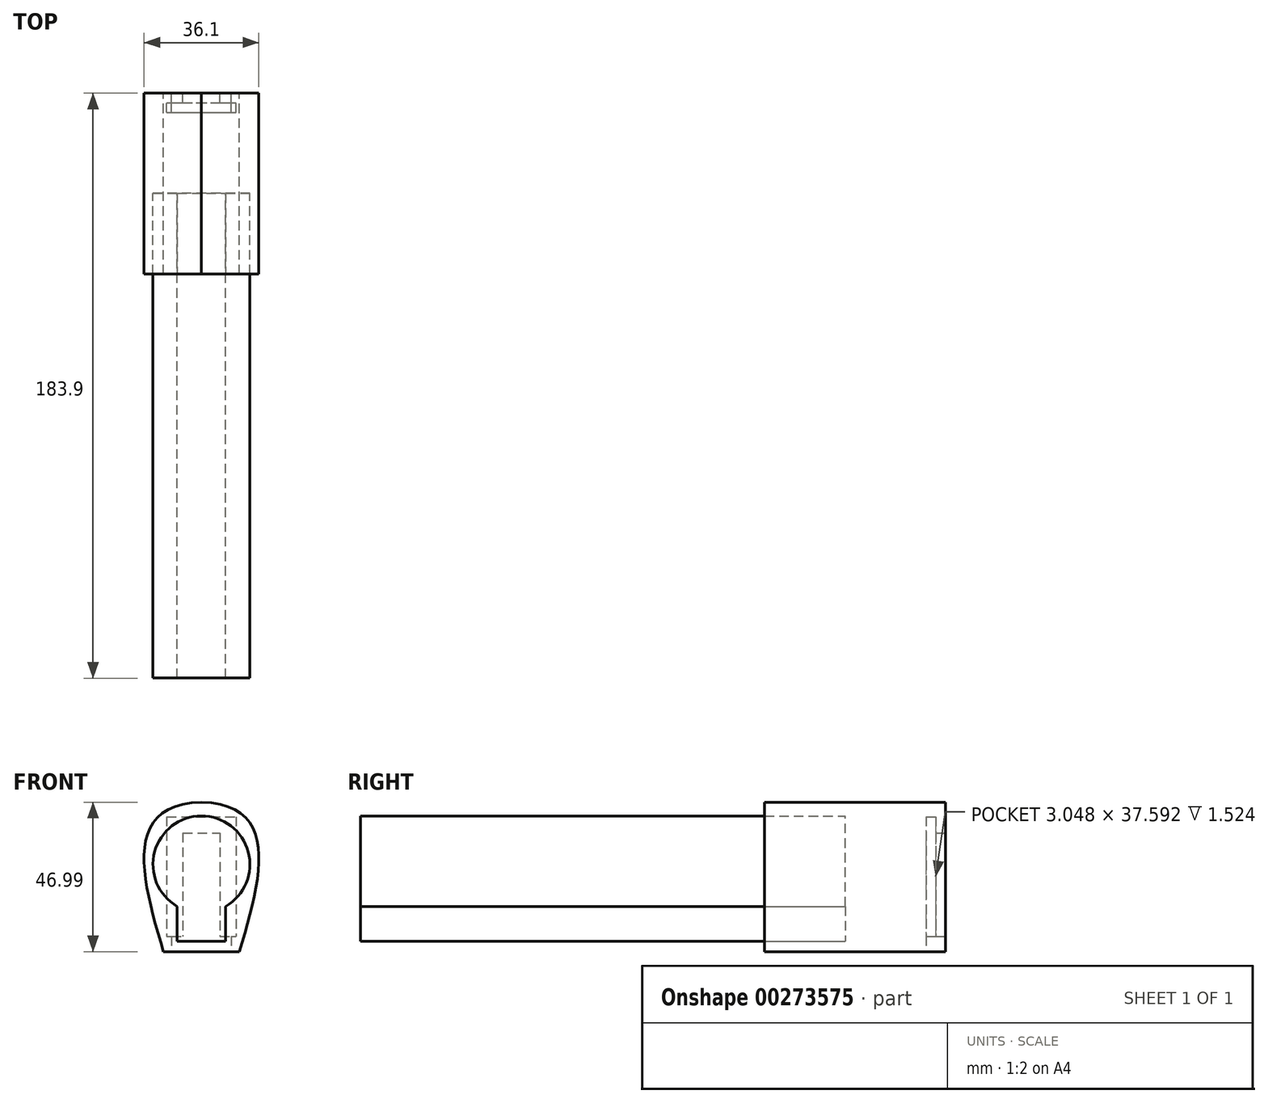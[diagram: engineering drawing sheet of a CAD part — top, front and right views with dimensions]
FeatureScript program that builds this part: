
annotation { "Feature Type Name" : "Feature", "Feature Type Description" : "" }
export const myFeature = defineFeature(function(context is Context, id is Id, definition is map)
    precondition{}
    {
        {
            var Q0;
            Q0=qCreatedBy(makeId("Front.planeOp"),FACE);
            var sketch = newSketch(context, id + "F0", { "sketchPlane" : qUnion([Q0])});
            skLineSegment(sketch, "E0.bottom", {"start": v(-5.84, 16.26) * mm, "end": v(5.84, 16.26) * mm});
            skLineSegment(sketch, "E0.top", {"start": v(-5.84, -16.26) * mm, "end": v(5.84, -16.26) * mm});
            skLineSegment(sketch, "E0.left", {"start": v(-5.84, 16.26) * mm, "end": v(-5.84, -16.26) * mm});
            skLineSegment(sketch, "E0.right", {"start": v(5.84, 16.26) * mm, "end": v(5.84, -16.26) * mm});
            skPoint(sketch, "E0.middle", {"position": v(0, 0) * mm});
            skLineSegment(sketch, "E1.bottom", {"start": v(-9.4, -16.26) * mm, "end": v(9.4, -16.26) * mm});
            skLineSegment(sketch, "E1.top", {"start": v(-9.4, -21.08) * mm, "end": v(9.4, -21.08) * mm});
            skLineSegment(sketch, "E1.left", {"start": v(-9.4, -16.26) * mm, "end": v(-9.4, -21.08) * mm});
            skLineSegment(sketch, "E1.right", {"start": v(9.4, -16.26) * mm, "end": v(9.4, -21.08) * mm});
            skPoint(sketch, "E1.middle", {"position": v(0, -18.67) * mm});
            skLineSegment(sketch, "E2", {"start": v(-8.6, 25.9) * mm, "end": v(11.39, 25.9) * mm, "construction": true});
            skLineSegment(sketch, "E3", {"start": v(-9.4, -21.08) * mm, "end": v(-11.94, -21.08) * mm});
            skFitSpline(sketch, "E4", {"points": [v(-11.94, -21.08) * mm, v(0, 25.9) * mm], "startDerivative": vector(-19.85, 66.84) * mm, "endDerivative": vector(76.2, 2.26) * mm});
            skFitSpline(sketch, "E5.MirrorCS", {"points": [v(11.94, -21.08) * mm, v(0, 25.9) * mm], "startDerivative": vector(19.85, 66.84) * mm, "endDerivative": vector(-76.2, 2.26) * mm});
            skLineSegment(sketch, "E6.MirrorCS", {"start": v(9.4, -21.08) * mm, "end": v(11.94, -21.08) * mm});
            skSolve(sketch);
        }
        {
            var Q0;
            Q0=makeQuery(id+"F0.imprint","IMPRINT",FACE,{"disambiguationData":[TD([[makeQuery(id+"F0.imprint","IMPRINT",EDGE,{"derivedFrom":sQuery(id+"F0.wireOp",EDGE,"E0.bottom")}),1.0]])]});
            extrude(context, id + "F1", {"entities" : qUnion([Q0]), "depth" : 3.05 * mm});
        }
        {
            var Q0;
            Q0=makeQuery(id+"F1.opExtrude","CAP_FACE",FACE,{"disambiguationData":[OSD([sQuery(id+"F0.wireOp",EDGE,"E0.bottom"),sQuery(id+"F0.wireOp",EDGE,"E0.left"),sQuery(id+"F0.wireOp",EDGE,"E0.right"),sQuery(id+"F0.wireOp",EDGE,"E1.bottom"),sQuery(id+"F0.wireOp",EDGE,"E1.left"),sQuery(id+"F0.wireOp",EDGE,"E1.right"),sQuery(id+"F0.wireOp",EDGE,"E3"),sQuery(id+"F0.wireOp",EDGE,"E4"),sQuery(id+"F0.wireOp",EDGE,"E5.MirrorCS"),sQuery(id+"F0.wireOp",EDGE,"E6.MirrorCS")])],"isStart":false});
            var sketch = newSketch(context, id + "F2", { "sketchPlane" : qUnion([Q0])});
            skLineSegment(sketch, "E7.bottom", {"start": v(-10.92, 21.34) * mm, "end": v(10.92, 21.34) * mm});
            skLineSegment(sketch, "E7.top", {"start": v(-10.92, -16.26) * mm, "end": v(10.92, -16.26) * mm});
            skLineSegment(sketch, "E7.left", {"start": v(-10.92, 21.34) * mm, "end": v(-10.92, -16.26) * mm});
            skLineSegment(sketch, "E7.right", {"start": v(10.92, 21.34) * mm, "end": v(10.92, -16.26) * mm});
            skSolve(sketch);
        }
        {
            var Q0;
            Q0=makeQuery(id+"F2.imprint","IMPRINT",FACE,{"disambiguationData":[TD([[makeQuery(id+"F2.imprint","IMPRINT",EDGE,{"derivedFrom":sQuery(id+"F2.wireOp",EDGE,"E7.bottom")}),1.0]])]});
            extrude(context, id + "F3", {"entities" : qUnion([Q0]), "operationType" : NewBodyOperationType.ADD, "depth" : 3.05 * mm});
        }
        {
            var Q0;
            Q0=makeQuery(id+"F3.opExtrude","CAP_FACE",FACE,{"disambiguationData":[OSD([sQuery(id+"F0.wireOp",EDGE,"E1.left"),sQuery(id+"F0.wireOp",EDGE,"E1.right"),sQuery(id+"F0.wireOp",EDGE,"E3"),sQuery(id+"F0.wireOp",EDGE,"E4"),sQuery(id+"F0.wireOp",EDGE,"E5.MirrorCS"),sQuery(id+"F0.wireOp",EDGE,"E6.MirrorCS"),sQuery(id+"F2.wireOp",EDGE,"E7.bottom"),sQuery(id+"F2.wireOp",EDGE,"E7.top"),sQuery(id+"F2.wireOp",EDGE,"E7.left"),sQuery(id+"F2.wireOp",EDGE,"E7.right")])],"isStart":false});
            var sketch = newSketch(context, id + "F4", { "sketchPlane" : qUnion([Q0])});
            skLineSegment(sketch, "E8", {"start": v(-9.4, -21.08) * mm, "end": v(9.4, -21.08) * mm});
            skSolve(sketch);
        }
        {
            var Q0;
            Q0=makeQuery(id+"F4.imprint","IMPRINT",FACE,{"disambiguationData":[TD([[makeQuery(id+"F4.imprint","IMPRINT",EDGE,{"derivedFrom":makeQuery(id+"F3.opExtrude","CAP_EDGE",EDGE,{"disambiguationData":[OSD([sQuery(id+"F2.wireOp",EDGE,"E7.bottom")])],"isStart":false})}),1.0]])]});
            var Q1;
            Q1=makeQuery(id+"F4.imprint","IMPRINT",FACE,{"disambiguationData":[TD([[makeQuery(id+"F4.imprint","IMPRINT",EDGE,{"derivedFrom":sQuery(id+"F4.wireOp",EDGE,"E8")}),1.0]])]});
            extrude(context, id + "F5", {"entities" : qUnion([Q0, Q1]), "operationType" : NewBodyOperationType.ADD, "depth" : 50.8 * mm});
        }
        {
            var Q0;
            Q0=makeQuery(id+"F5.opExtrude","CAP_FACE",FACE,{"disambiguationData":[OSD([sQuery(id+"F0.wireOp",EDGE,"E3"),sQuery(id+"F0.wireOp",EDGE,"E4"),sQuery(id+"F0.wireOp",EDGE,"E5.MirrorCS"),sQuery(id+"F0.wireOp",EDGE,"E6.MirrorCS"),sQuery(id+"F4.wireOp",EDGE,"E8")])],"isStart":false});
            var sketch = newSketch(context, id + "F6", { "sketchPlane" : qUnion([Q0])});
            skArc(sketch, "E9", {"start": v(7.62, -6.85) * mm, "mid": v(0, 21.59) * mm, "end": v(-7.62, -6.85) * mm});
            skLineSegment(sketch, "E10.top", {"start": v(-7.62, -17.78) * mm, "end": v(7.62, -17.78) * mm});
            skLineSegment(sketch, "E10.left", {"start": v(-7.62, -6.85) * mm, "end": v(-7.62, -17.78) * mm});
            skLineSegment(sketch, "E10.right", {"start": v(7.62, -6.85) * mm, "end": v(7.62, -17.78) * mm});
            skPoint(sketch, "E10.middle", {"position": v(0, -8.9) * mm});
            skPoint(sketch, "E11.orphan", {"position": v(7.62, 0) * mm});
            skPoint(sketch, "E12.orphan", {"position": v(-7.62, 0) * mm});
            skSolve(sketch);
        }
        {
            var Q0;
            Q0=makeQuery(id+"F6.imprint","IMPRINT",FACE,{"disambiguationData":[TD([[makeQuery(id+"F6.imprint","IMPRINT",EDGE,{"derivedFrom":sQuery(id+"F6.wireOp",EDGE,"E9")}),1.0]])]});
            extrude(context, id + "F7", {"entities" : qUnion([Q0]), "operationType" : NewBodyOperationType.REMOVE, "oppositeDirection" : true, "depth" : 25.4 * mm});
        }
        {
            var Q0;
            Q0=makeQuery(id+"F7.boolean.opBoolean","COPY",FACE,{"derivedFrom":makeQuery(id+"F7.opExtrude","CAP_FACE",FACE,{"disambiguationData":[OSD([sQuery(id+"F6.wireOp",EDGE,"E9"),sQuery(id+"F6.wireOp",EDGE,"E10.top"),sQuery(id+"F6.wireOp",EDGE,"E10.left"),sQuery(id+"F6.wireOp",EDGE,"E10.right")])],"isStart":false})});
            extrude(context, id + "F8", {"entities" : qUnion([Q0]), "depth" : 152.4 * mm, "offsetDistance" : 25.4 * mm});
        }
    });
